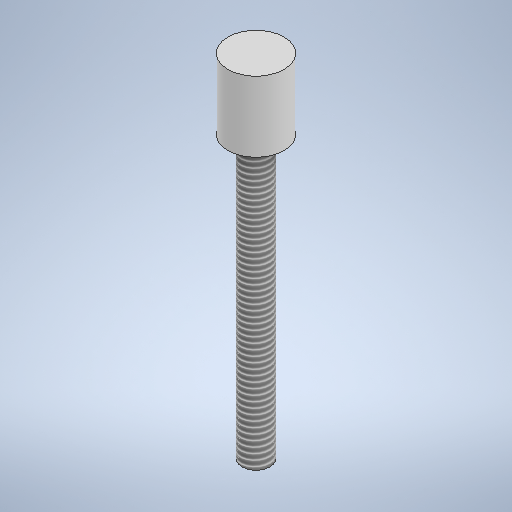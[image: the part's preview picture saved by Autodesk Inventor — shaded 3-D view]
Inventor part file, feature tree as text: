
AUTODESK INVENTOR PART (.ipt)
format: ipt  version: 2025.2 (Build 292293000, 293)  size: 260,096 bytes
history: native  units: mm
features: extrude x2, sketch x2, other x1, thread x1
ambient origin geometry x8: Origin, YZ Plane, XZ Plane, XY Plane, X Axis, Y Axis, Z Axis, Center Point
bodies: Body1 (feature_tree)
feature tree (6):
  other  "Bryła1"
  extrude  "Wyciągnięcie proste1"  Depth=4.0mm
  extrude  "Wyciągnięcie proste2"  Depth=5.0mm TaperAngle=0.0deg
  thread  "Gwint1"
  sketch  "Szkic1"
  sketch  "Szkic2"
